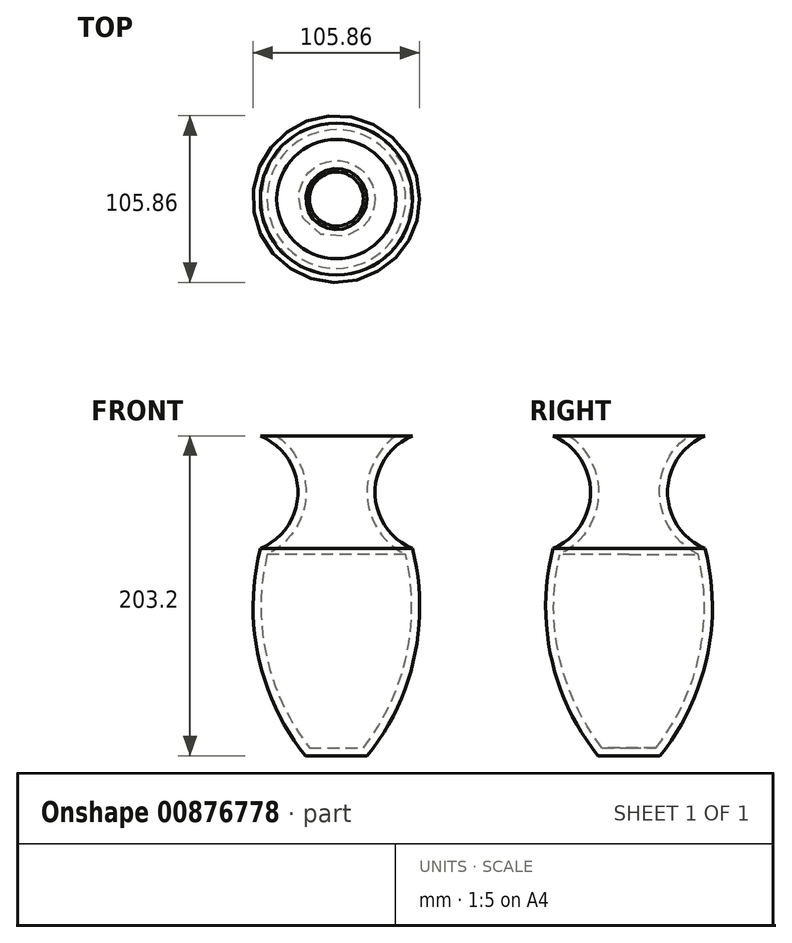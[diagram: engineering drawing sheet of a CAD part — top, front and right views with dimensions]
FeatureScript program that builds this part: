
annotation { "Feature Type Name" : "Feature", "Feature Type Description" : "" }
export const myFeature = defineFeature(function(context is Context, id is Id, definition is map)
    precondition{}
    {
        {
            var Q0;
            Q0=qCreatedBy(makeId("Front.planeOp"),FACE);
            var sketch = newSketch(context, id + "F0", { "sketchPlane" : qUnion([Q0])});
            skLineSegment(sketch, "E0", {"start": v(0, 71.56) * mm, "end": v(0, -131.64) * mm});
            skLineSegment(sketch, "E1", {"start": v(-19.59, -131.64) * mm, "end": v(0, -131.64) * mm});
            skLineSegment(sketch, "E2", {"start": v(0, 71.56) * mm, "end": v(-48.33, 71.56) * mm});
            skArc(sketch, "E3", {"start": v(-48.33, 0) * mm, "mid": v(-24.46, 35.78) * mm, "end": v(-48.33, 71.56) * mm});
            skArc(sketch, "E4", {"start": v(-48.33, 0) * mm, "mid": v(-49.45, -69.2) * mm, "end": v(-19.59, -131.64) * mm});
            skSolve(sketch);
        }
        {
            var Q0;
            Q0=makeQuery(id+"F0.imprint","IMPRINT",FACE,{"disambiguationData":[TD([[makeQuery(id+"F0.imprint","IMPRINT",EDGE,{"derivedFrom":sQuery(id+"F0.wireOp",EDGE,"E0")}),-1.0]])]});
            var Q1;
            Q1=sQuery(id+"F0.wireOp",EDGE,"E0");
            revolve(context, id + "F1", {"surfaceOperationType" : NewSurfaceOperationType.NEW, "entities" : qUnion([Q0]), "axis" : qUnion([Q1]), "revolveType" : RevolveType.FULL});
        }
        {
            var Q0;
            Q0=makeQuery(id+"F1.opRevolve","SWEPT_FACE",FACE,{"disambiguationData":[OSD([sQuery(id+"F0.wireOp",EDGE,"E2")])]});
            shell(context, id + "F2", {"entities" : qUnion([Q0]), "thickness" : 5.08 * mm});
        }
    });
